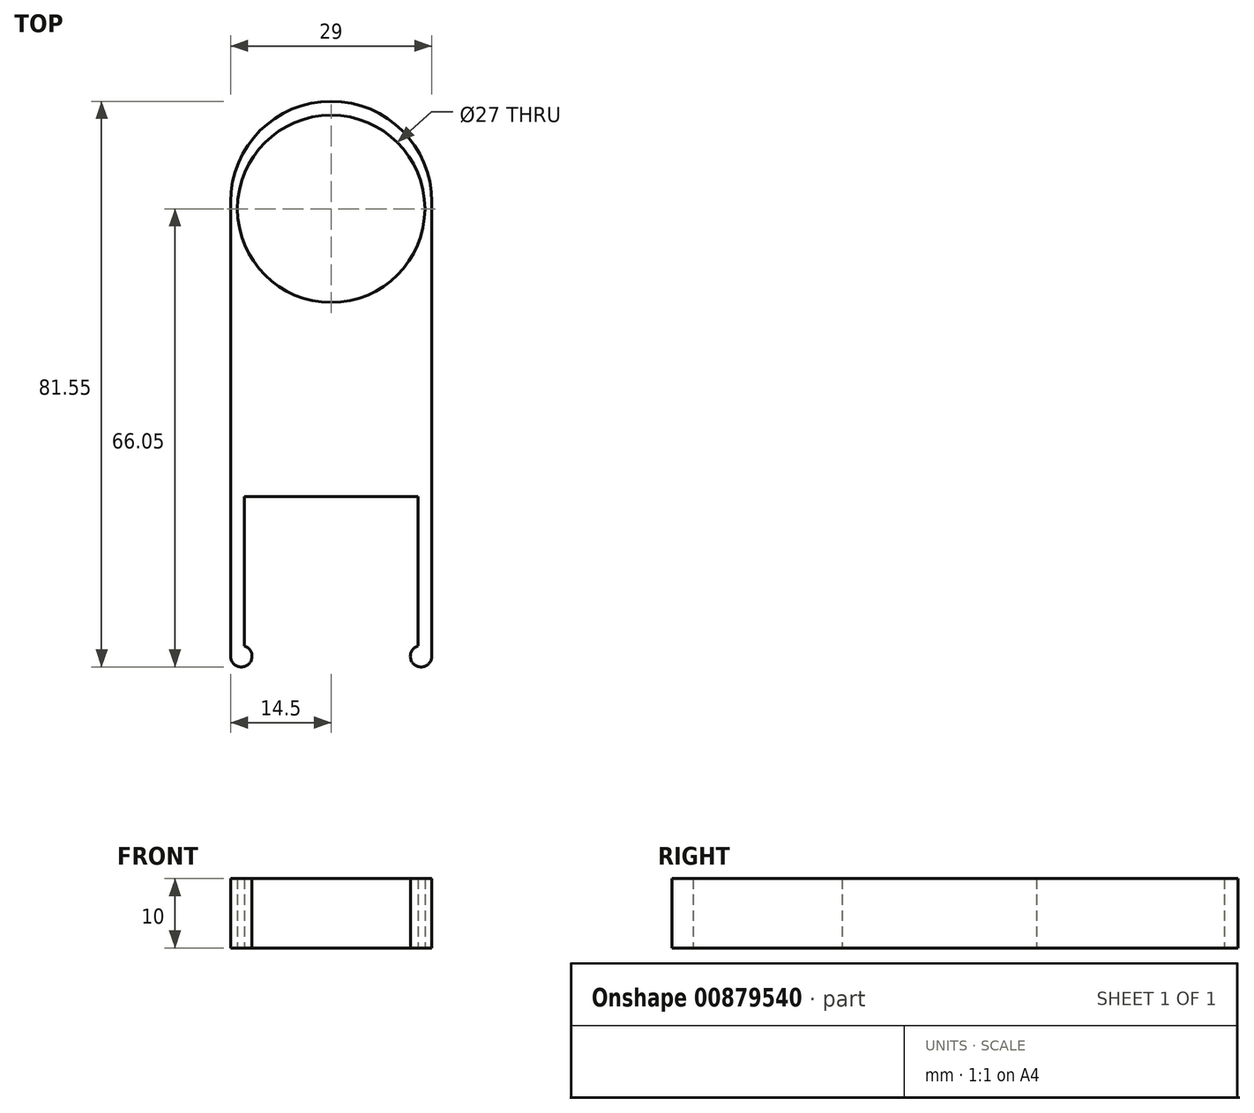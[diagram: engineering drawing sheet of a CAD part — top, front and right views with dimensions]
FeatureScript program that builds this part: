
annotation { "Feature Type Name" : "Feature", "Feature Type Description" : "" }
export const myFeature = defineFeature(function(context is Context, id is Id, definition is map)
    precondition{}
    {
        {
            var Q0;
            Q0=qCreatedBy(makeId("Top.planeOp"),FACE);
            var sketch = newSketch(context, id + "F0", { "sketchPlane" : qUnion([Q0])});
            skLineSegment(sketch, "E0.bottom", {"start": v(12.5, 0) * mm, "end": v(14.5, 0) * mm});
            skLineSegment(sketch, "E0.top", {"start": v(12.5, -23) * mm, "end": v(14.5, -23) * mm});
            skLineSegment(sketch, "E0.left", {"start": v(12.5, 0) * mm, "end": v(12.5, -23) * mm});
            skLineSegment(sketch, "E0.right", {"start": v(14.5, 0) * mm, "end": v(14.5, -23) * mm});
            skLineSegment(sketch, "E1.bottom", {"start": v(14.5, 0) * mm, "end": v(-14.5, 0) * mm});
            skLineSegment(sketch, "E1.top", {"start": v(14.5, 28) * mm, "end": v(-14.5, 28) * mm});
            skLineSegment(sketch, "E1.left", {"start": v(14.5, 0) * mm, "end": v(14.5, 28) * mm});
            skLineSegment(sketch, "E1.right", {"start": v(-14.5, 0) * mm, "end": v(-14.5, 28) * mm});
            skCircle(sketch, "E2", {"center": v(12.95, -23) * mm, "radius": 1.55 * mm});
            skPoint(sketch, "E3", {"position": v(14.5, -23) * mm});
            skPoint(sketch, "E4", {"position": v(0, 0) * mm});
            skLineSegment(sketch, "E5.bottom", {"start": v(-14.5, 0) * mm, "end": v(-12.5, 0) * mm});
            skLineSegment(sketch, "E5.top", {"start": v(-14.5, -23) * mm, "end": v(-12.5, -23) * mm});
            skLineSegment(sketch, "E5.left", {"start": v(-14.5, 0) * mm, "end": v(-14.5, -23) * mm});
            skLineSegment(sketch, "E5.right", {"start": v(-12.5, 0) * mm, "end": v(-12.5, -23) * mm});
            skCircle(sketch, "E6", {"center": v(-12.95, -23) * mm, "radius": 1.55 * mm});
            skPoint(sketch, "E7", {"position": v(-14.5, -23) * mm});
            skCircle(sketch, "E8", {"center": v(0, 42.5) * mm, "radius": 14.5 * mm});
            skPoint(sketch, "E9", {"position": v(0, 28) * mm});
            skPoint(sketch, "E10", {"position": v(-14.5, 42.5) * mm});
            skLineSegment(sketch, "E11", {"start": v(-14.5, 28) * mm, "end": v(-14.5, 42.5) * mm});
            skPoint(sketch, "E12", {"position": v(14.5, 42.5) * mm});
            skLineSegment(sketch, "E13", {"start": v(14.5, 28) * mm, "end": v(14.5, 42.5) * mm});
            skSolve(sketch);
        }
        {
            var Q0;
            Q0=qCreatedBy(makeId("Top.planeOp"),FACE);
            var sketch = newSketch(context, id + "F1", { "sketchPlane" : qUnion([Q0])});
            skCircle(sketch, "E14", {"center": v(0, 41.5) * mm, "radius": 13.5 * mm});
            skPoint(sketch, "E15", {"position": v(0, 57) * mm});
            skPoint(sketch, "E16", {"position": v(0, 55) * mm});
            skSolve(sketch);
        }
        {
            var Q0;
            Q0 = qSketchRegion(id + "F0", true);
            extrude(context, id + "F2", {"entities" : qUnion([Q0]), "depth" : 10 * mm, "offsetDistance" : 25 * mm});
        }
        {
            var Q0;
            Q0 = qSketchRegion(id + "F1", true);
            extrude(context, id + "F3", {"entities" : qUnion([Q0]), "operationType" : NewBodyOperationType.REMOVE, "depth" : 10 * mm, "offsetDistance" : 25 * mm});
        }
    });
